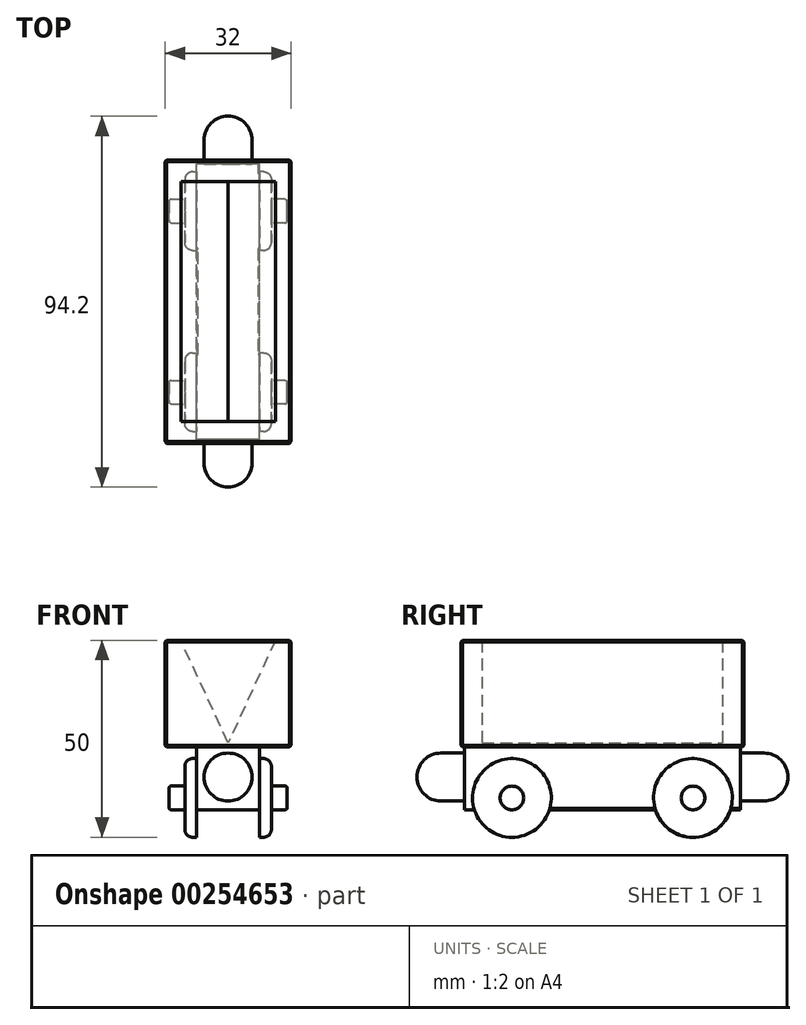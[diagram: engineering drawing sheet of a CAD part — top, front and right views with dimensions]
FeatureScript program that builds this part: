
annotation { "Feature Type Name" : "Feature", "Feature Type Description" : "" }
export const myFeature = defineFeature(function(context is Context, id is Id, definition is map)
    precondition{}
    {
        {
            var Q0;
            Q0=qCreatedBy(makeId("Front.planeOp"),FACE);
            var sketch = newSketch(context, id + "F0", { "sketchPlane" : qUnion([Q0])});
            skLineSegment(sketch, "E0.bottom", {"start": v(16, 13.5) * mm, "end": v(-16, 13.5) * mm});
            skLineSegment(sketch, "E0.top", {"start": v(16, -13.5) * mm, "end": v(-16, -13.5) * mm});
            skLineSegment(sketch, "E0.left", {"start": v(16, 13.5) * mm, "end": v(16, -13.5) * mm});
            skLineSegment(sketch, "E0.right", {"start": v(-16, 13.5) * mm, "end": v(-16, -13.5) * mm});
            skPoint(sketch, "E0.middle", {"position": v(0, 0) * mm});
            skSolve(sketch);
        }
        {
            var Q0;
            Q0 = qSketchRegion(id + "F0", true);
            extrude(context, id + "F1", {"entities" : qUnion([Q0]), "endBound" : BoundingType.SYMMETRIC, "depth" : 72 * mm});
        }
        {
            var Q0;
            Q0=makeQuery(id+"F1.opExtrude","SWEPT_FACE",FACE,{"disambiguationData":[OSD([sQuery(id+"F0.wireOp",EDGE,"E0.top")])]});
            var sketch = newSketch(context, id + "F2", { "sketchPlane" : qUnion([Q0])});
            skLineSegment(sketch, "E1.bottom", {"start": v(8, 35) * mm, "end": v(-8, 35) * mm});
            skLineSegment(sketch, "E1.top", {"start": v(8, -35) * mm, "end": v(-8, -35) * mm});
            skLineSegment(sketch, "E1.left", {"start": v(8, 35) * mm, "end": v(8, -35) * mm});
            skLineSegment(sketch, "E1.right", {"start": v(-8, 35) * mm, "end": v(-8, -35) * mm});
            skPoint(sketch, "E1.middle", {"position": v(0, 0) * mm});
            skSolve(sketch);
        }
        {
            var Q0;
            Q0 = qSketchRegion(id + "F2", true);
            extrude(context, id + "F3", {"entities" : qUnion([Q0]), "operationType" : NewBodyOperationType.ADD, "depth" : 16 * mm});
        }
        {
            var Q0;
            Q0=makeQuery(id+"F3.opExtrude","SWEPT_FACE",FACE,{"disambiguationData":[OSD([sQuery(id+"F2.wireOp",EDGE,"E1.bottom")])]});
            var sketch = newSketch(context, id + "F4", { "sketchPlane" : qUnion([Q0])});
            skCircle(sketch, "E2", {"center": v(0, -21.2) * mm, "radius": 6.1 * mm});
            skSolve(sketch);
        }
        {
            var Q0;
            Q0=makeQuery(id+"F4.imprint","IMPRINT",FACE,{"disambiguationData":[TD([[makeQuery(id+"F4.imprint","IMPRINT",EDGE,{"derivedFrom":sQuery(id+"F4.wireOp",EDGE,"E2")}),1.0]])]});
            extrude(context, id + "F5", {"entities" : qUnion([Q0]), "operationType" : NewBodyOperationType.ADD, "depth" : 6 * mm});
        }
        {
            var Q0;
            Q0=makeQuery(id+"F3.opExtrude","SWEPT_FACE",FACE,{"disambiguationData":[OSD([sQuery(id+"F2.wireOp",EDGE,"E1.top")])]});
            var sketch = newSketch(context, id + "F6", { "sketchPlane" : qUnion([Q0])});
            skCircle(sketch, "E3", {"center": v(0, -21.2) * mm, "radius": 6.1 * mm});
            skSolve(sketch);
        }
        {
            var Q0;
            Q0 = qSketchRegion(id + "F6", true);
            extrude(context, id + "F7", {"entities" : qUnion([Q0]), "operationType" : NewBodyOperationType.ADD, "depth" : 6 * mm});
        }
        {
            var Q0;
            Q0=makeQuery(id+"F5.opExtrude","CAP_FACE",FACE,{"disambiguationData":[OSD([sQuery(id+"F4.wireOp",EDGE,"E2")])],"isStart":false});
            var sketch = newSketch(context, id + "F8", { "sketchPlane" : qUnion([Q0])});
            skLineSegment(sketch, "E4", {"start": v(0, -15.1) * mm, "end": v(0, -27.3) * mm});
            skSolve(sketch);
        }
        {
            var Q0;
            {var subQ0=sQuery(id+"F8.wireOp",EDGE,"E4");Q0=makeQuery(id+"F8.imprint","IMPRINT",FACE,{"disambiguationData":[TD([[makeQuery(id+"F8.imprint","IMPRINT",EDGE,{"derivedFrom":subQ0}),-1.0]])]});}
            var Q1;
            Q1=sQuery(id+"F8.wireOp",EDGE,"E4");
            revolve(context, id + "F9", {"operationType" : NewBodyOperationType.ADD, "entities" : qUnion([Q0]), "axis" : qUnion([Q1]), "revolveType" : RevolveType.FULL});
        }
        {
            var Q0;
            Q0=makeQuery(id+"F7.opExtrude","CAP_FACE",FACE,{"disambiguationData":[OSD([sQuery(id+"F6.wireOp",EDGE,"E3")])],"isStart":false});
            var sketch = newSketch(context, id + "F10", { "sketchPlane" : qUnion([Q0])});
            skLineSegment(sketch, "E5", {"start": v(0, -15.1) * mm, "end": v(0, -27.3) * mm});
            skSolve(sketch);
        }
        {
            var Q0;
            {var subQ0=sQuery(id+"F10.wireOp",EDGE,"E5");Q0=makeQuery(id+"F10.imprint","IMPRINT",FACE,{"disambiguationData":[TD([[makeQuery(id+"F10.imprint","IMPRINT",EDGE,{"derivedFrom":subQ0}),-1.0]])]});}
            var Q1;
            Q1=sQuery(id+"F10.wireOp",EDGE,"E5");
            revolve(context, id + "F11", {"operationType" : NewBodyOperationType.ADD, "entities" : qUnion([Q0]), "axis" : qUnion([Q1]), "revolveType" : RevolveType.FULL});
        }
        {
            var Q0;
            Q0=makeQuery(id+"F3.opExtrude","SWEPT_FACE",FACE,{"disambiguationData":[OSD([sQuery(id+"F2.wireOp",EDGE,"E1.left")])]});
            var sketch = newSketch(context, id + "F12", { "sketchPlane" : qUnion([Q0])});
            skCircle(sketch, "E6", {"center": v(23, -26.5) * mm, "radius": 10 * mm});
            skSolve(sketch);
        }
        {
            var Q0;
            Q0 = qSketchRegion(id + "F12", true);
            extrude(context, id + "F13", {"entities" : qUnion([Q0]), "operationType" : NewBodyOperationType.ADD, "depth" : 3 * mm});
        }
        {
            var Q0;
            Q0=makeQuery(id+"F1.opExtrude","SWEPT_BODY",BODY,{"disambiguationData":[OSD([sQuery(id+"F0.wireOp",EDGE,"E0.bottom"),sQuery(id+"F0.wireOp",EDGE,"E0.top"),sQuery(id+"F0.wireOp",EDGE,"E0.left"),sQuery(id+"F0.wireOp",EDGE,"E0.right")])]});
            var Q1;
            Q1=qCreatedBy(makeId("Front.planeOp"),FACE);
            mirror(context, id + "F14", {"operationType" : NewBodyOperationType.ADD, "entities" : qUnion([Q0]), "mirrorPlane" : qUnion([Q1])});
        }
        {
            var Q0;
            Q0=makeQuery(id+"F1.opExtrude","SWEPT_BODY",BODY,{"disambiguationData":[OSD([sQuery(id+"F0.wireOp",EDGE,"E0.bottom"),sQuery(id+"F0.wireOp",EDGE,"E0.top"),sQuery(id+"F0.wireOp",EDGE,"E0.left"),sQuery(id+"F0.wireOp",EDGE,"E0.right")])]});
            var Q1;
            Q1=qCreatedBy(makeId("Right.planeOp"),FACE);
            mirror(context, id + "F15", {"operationType" : NewBodyOperationType.ADD, "entities" : qUnion([Q0]), "mirrorPlane" : qUnion([Q1])});
        }
        {
            var Q0;
            Q0=makeQuery(id+"F1.opExtrude","SWEPT_FACE",FACE,{"disambiguationData":[OSD([sQuery(id+"F0.wireOp",EDGE,"E0.bottom")])]});
            var sketch = newSketch(context, id + "F16", { "sketchPlane" : qUnion([Q0])});
            skLineSegment(sketch, "E7.bottom", {"start": v(12, 30.5) * mm, "end": v(-12, 30.5) * mm});
            skLineSegment(sketch, "E7.top", {"start": v(12, -30.5) * mm, "end": v(-12, -30.5) * mm});
            skLineSegment(sketch, "E7.left", {"start": v(12, 30.5) * mm, "end": v(12, -30.5) * mm});
            skLineSegment(sketch, "E7.right", {"start": v(-12, 30.5) * mm, "end": v(-12, -30.5) * mm});
            skPoint(sketch, "E7.middle", {"position": v(0, 0) * mm});
            skSolve(sketch);
        }
        {
            var Q0;
            Q0 = qSketchRegion(id + "F16", true);
            extrude(context, id + "F17", {"entities" : qUnion([Q0]), "operationType" : NewBodyOperationType.REMOVE, "oppositeDirection" : true, "depth" : 26 * mm});
        }
        {
            var Q0;
            Q0=makeQuery(id+"F14.opPattern","COPY",FACE,{"derivedFrom":makeQuery(id+"F13.opExtrude","CAP_FACE",FACE,{"disambiguationData":[OSD([sQuery(id+"F12.wireOp",EDGE,"E6")])],"isStart":false}),"instanceName":"1"});
            var sketch = newSketch(context, id + "F18", { "sketchPlane" : qUnion([Q0])});
            skCircle(sketch, "E8", {"center": v(-23, -26.5) * mm, "radius": 3 * mm});
            skSolve(sketch);
        }
        {
            var Q0;
            Q0=makeQuery(id+"F18.imprint","IMPRINT",FACE,{"disambiguationData":[TD([[makeQuery(id+"F18.imprint","IMPRINT",EDGE,{"derivedFrom":sQuery(id+"F18.wireOp",EDGE,"E8")}),1.0]])]});
            extrude(context, id + "F19", {"entities" : qUnion([Q0]), "operationType" : NewBodyOperationType.ADD, "depth" : 4 * mm});
        }
        {
            var Q0;
            Q0=makeQuery(id+"F1.opExtrude","SWEPT_BODY",BODY,{"disambiguationData":[OSD([sQuery(id+"F0.wireOp",EDGE,"E0.bottom"),sQuery(id+"F0.wireOp",EDGE,"E0.top"),sQuery(id+"F0.wireOp",EDGE,"E0.left"),sQuery(id+"F0.wireOp",EDGE,"E0.right")])]});
            var Q1;
            Q1=qCreatedBy(makeId("Front.planeOp"),FACE);
            mirror(context, id + "F20", {"operationType" : NewBodyOperationType.ADD, "entities" : qUnion([Q0]), "mirrorPlane" : qUnion([Q1])});
        }
        {
            var Q0;
            Q0=makeQuery(id+"F1.opExtrude","SWEPT_BODY",BODY,{"disambiguationData":[OSD([sQuery(id+"F0.wireOp",EDGE,"E0.bottom"),sQuery(id+"F0.wireOp",EDGE,"E0.top"),sQuery(id+"F0.wireOp",EDGE,"E0.left"),sQuery(id+"F0.wireOp",EDGE,"E0.right")])]});
            var Q1;
            Q1=qCreatedBy(makeId("Right.planeOp"),FACE);
            mirror(context, id + "F21", {"operationType" : NewBodyOperationType.ADD, "entities" : qUnion([Q0]), "mirrorPlane" : qUnion([Q1])});
        }
        {
            var Q0;
            Q0=makeQuery(id+"F17.boolean.opBoolean","COPY",FACE,{"derivedFrom":makeQuery(id+"F17.opExtrude","SWEPT_FACE",FACE,{"disambiguationData":[OSD([sQuery(id+"F16.wireOp",EDGE,"E7.bottom")])]})});
            var sketch = newSketch(context, id + "F22", { "sketchPlane" : qUnion([Q0])});
            skLineSegment(sketch, "E9", {"start": v(-12, 13.5) * mm, "end": v(-12, -12.5) * mm});
            skLineSegment(sketch, "E10", {"start": v(-12, -12.5) * mm, "end": v(0, -12.5) * mm});
            skLineSegment(sketch, "E11", {"start": v(0, -12.5) * mm, "end": v(-12, 13.5) * mm});
            skLineSegment(sketch, "E12", {"start": v(0, -12.5) * mm, "end": v(12, -12.5) * mm});
            skLineSegment(sketch, "E13", {"start": v(12, -12.5) * mm, "end": v(12, 13.5) * mm});
            skLineSegment(sketch, "E14", {"start": v(12, 13.5) * mm, "end": v(0, -12.5) * mm});
            skSolve(sketch);
        }
        {
            var Q0;
            Q0 = qSketchRegion(id + "F22", true);
            extrude(context, id + "F23", {"entities" : qUnion([Q0]), "operationType" : NewBodyOperationType.ADD, "endBound" : BoundingType.UP_TO_NEXT, "depth" : 25 * mm});
        }
        {
            var Q0;
            Q0=makeQuery(id+"F19.opExtrude","CAP_EDGE",EDGE,{"disambiguationData":[OSD([sQuery(id+"F18.wireOp",EDGE,"E8")])],"isStart":false});
            var Q1;
            Q1=makeQuery(id+"F20.opPattern","COPY",EDGE,{"derivedFrom":makeQuery(id+"F19.opExtrude","CAP_EDGE",EDGE,{"disambiguationData":[OSD([sQuery(id+"F18.wireOp",EDGE,"E8")])],"isStart":false}),"instanceName":"1"});
            var Q2;
            Q2=makeQuery(id+"F21.opPattern","COPY",EDGE,{"derivedFrom":makeQuery(id+"F20.opPattern","COPY",EDGE,{"derivedFrom":makeQuery(id+"F19.opExtrude","CAP_EDGE",EDGE,{"disambiguationData":[OSD([sQuery(id+"F18.wireOp",EDGE,"E8")])],"isStart":false}),"instanceName":"1"}),"instanceName":"1"});
            var Q3;
            Q3=makeQuery(id+"F21.opPattern","COPY",EDGE,{"derivedFrom":makeQuery(id+"F19.opExtrude","CAP_EDGE",EDGE,{"disambiguationData":[OSD([sQuery(id+"F18.wireOp",EDGE,"E8")])],"isStart":false}),"instanceName":"1"});
            fillet(context, id + "F24", {"entities" : qUnion([Q0, Q1, Q2, Q3]), "radius" : 0.5 * mm, "tangentPropagation" : true, "allowEdgeOverflow" : false});
        }
        {
            var Q0;
            Q0=makeQuery(id+"F14.opPattern","COPY",EDGE,{"derivedFrom":makeQuery(id+"F13.opExtrude","CAP_EDGE",EDGE,{"disambiguationData":[OSD([sQuery(id+"F12.wireOp",EDGE,"E6")])],"isStart":false}),"instanceName":"1"});
            var Q1;
            Q1=makeQuery(id+"F13.opExtrude","CAP_EDGE",EDGE,{"disambiguationData":[OSD([sQuery(id+"F12.wireOp",EDGE,"E6")])],"isStart":false});
            var Q2;
            Q2=makeQuery(id+"F15.opPattern","COPY",EDGE,{"derivedFrom":makeQuery(id+"F13.opExtrude","CAP_EDGE",EDGE,{"disambiguationData":[OSD([sQuery(id+"F12.wireOp",EDGE,"E6")])],"isStart":false}),"instanceName":"1"});
            var Q3;
            Q3=makeQuery(id+"F15.opPattern","COPY",EDGE,{"derivedFrom":makeQuery(id+"F14.opPattern","COPY",EDGE,{"derivedFrom":makeQuery(id+"F13.opExtrude","CAP_EDGE",EDGE,{"disambiguationData":[OSD([sQuery(id+"F12.wireOp",EDGE,"E6")])],"isStart":false}),"instanceName":"1"}),"instanceName":"1"});
            fillet(context, id + "F25", {"entities" : qUnion([Q0, Q1, Q2, Q3]), "radius" : 2 * mm, "tangentPropagation" : true, "allowEdgeOverflow" : false});
        }
        {
            var Q0;
            Q0=makeQuery(id+"F1.opExtrude","CAP_EDGE",EDGE,{"disambiguationData":[OSD([sQuery(id+"F0.wireOp",EDGE,"E0.right")])],"isStart":false});
            var Q1;
            Q1=makeQuery(id+"F1.opExtrude","CAP_EDGE",EDGE,{"disambiguationData":[OSD([sQuery(id+"F0.wireOp",EDGE,"E0.bottom")])],"isStart":false});
            var Q2;
            Q2=makeQuery(id+"F1.opExtrude","SWEPT_EDGE",EDGE,{"disambiguationData":[OSD([sQuery(id+"F0.wireOp",EDGE,"E0.bottom"),sQuery(id+"F0.wireOp",EDGE,"E0.right")])]});
            var Q3;
            Q3=makeQuery(id+"F1.opExtrude","CAP_EDGE",EDGE,{"disambiguationData":[OSD([sQuery(id+"F0.wireOp",EDGE,"E0.bottom")])],"isStart":true});
            var Q4;
            Q4=makeQuery(id+"F1.opExtrude","SWEPT_EDGE",EDGE,{"disambiguationData":[OSD([sQuery(id+"F0.wireOp",EDGE,"E0.bottom"),sQuery(id+"F0.wireOp",EDGE,"E0.left")])]});
            var Q5;
            Q5=makeQuery(id+"F1.opExtrude","CAP_EDGE",EDGE,{"disambiguationData":[OSD([sQuery(id+"F0.wireOp",EDGE,"E0.left")])],"isStart":false});
            var Q6;
            Q6=makeQuery(id+"F1.opExtrude","CAP_EDGE",EDGE,{"disambiguationData":[OSD([sQuery(id+"F0.wireOp",EDGE,"E0.top")])],"isStart":false});
            var Q7;
            Q7=makeQuery(id+"F1.opExtrude","SWEPT_EDGE",EDGE,{"disambiguationData":[OSD([sQuery(id+"F0.wireOp",EDGE,"E0.top"),sQuery(id+"F0.wireOp",EDGE,"E0.left")])]});
            var Q8;
            Q8=makeQuery(id+"F1.opExtrude","CAP_EDGE",EDGE,{"disambiguationData":[OSD([sQuery(id+"F0.wireOp",EDGE,"E0.left")])],"isStart":true});
            var Q9;
            Q9=makeQuery(id+"F1.opExtrude","CAP_FACE",FACE,{"disambiguationData":[OSD([sQuery(id+"F0.wireOp",EDGE,"E0.bottom"),sQuery(id+"F0.wireOp",EDGE,"E0.top"),sQuery(id+"F0.wireOp",EDGE,"E0.left"),sQuery(id+"F0.wireOp",EDGE,"E0.right")])],"isStart":true});
            var Q10;
            Q10=makeQuery(id+"F1.opExtrude","SWEPT_EDGE",EDGE,{"disambiguationData":[OSD([sQuery(id+"F0.wireOp",EDGE,"E0.top"),sQuery(id+"F0.wireOp",EDGE,"E0.right")])]});
            var Q11;
            {var subQ0=sQuery(id+"F12.wireOp",EDGE,"E6");var subQ1=makeQuery(id+"F13.opExtrude","CAP_FACE",FACE,{"disambiguationData":[OSD([subQ0])],"isStart":true});var subQ2=sQuery(id+"F2.wireOp",EDGE,"E1.right");var subQ3=makeQuery(id+"F13.opExtrude","SWEPT_FACE",FACE,{"disambiguationData":[OSD([subQ0])]});Q11=makeQuery(id+"F15.boolean.opBoolean","SPLIT",EDGE,{"disambiguationData":[TD([makeQuery(id+"F3.opExtrude","CAP_FACE",FACE,{"disambiguationData":[OSD([sQuery(id+"F2.wireOp",EDGE,"E1.bottom"),sQuery(id+"F2.wireOp",EDGE,"E1.top"),sQuery(id+"F2.wireOp",EDGE,"E1.left"),subQ2])],"isStart":false}),makeQuery(id+"F3.opExtrude","SWEPT_FACE",FACE,{"disambiguationData":[OSD([subQ2])]}),makeQuery(id+"F15.opPattern","COPY",FACE,{"derivedFrom":subQ3,"instanceName":"1"}),makeQuery(id+"F15.opPattern","COPY",FACE,{"derivedFrom":subQ1,"instanceName":"1"}),makeQuery(id+"F15.opPattern","COPY",FACE,{"derivedFrom":makeQuery(id+"F14.opPattern","COPY",FACE,{"derivedFrom":subQ3,"instanceName":"1"}),"instanceName":"1"}),makeQuery(id+"F15.opPattern","COPY",FACE,{"derivedFrom":makeQuery(id+"F14.opPattern","COPY",FACE,{"derivedFrom":subQ1,"instanceName":"1"}),"instanceName":"1"})])],"derivedFrom":makeQuery(id+"F3.opExtrude","CAP_EDGE",EDGE,{"disambiguationData":[OSD([subQ2])],"isStart":false})});}
            var Q12;
            {var subQ0=sQuery(id+"F12.wireOp",EDGE,"E6");var subQ1=makeQuery(id+"F13.opExtrude","CAP_FACE",FACE,{"disambiguationData":[OSD([subQ0])],"isStart":true});var subQ2=makeQuery(id+"F13.opExtrude","SWEPT_FACE",FACE,{"disambiguationData":[OSD([subQ0])]});var subQ3=sQuery(id+"F2.wireOp",EDGE,"E1.left");var subQ4=makeQuery(id+"F3.opExtrude","SWEPT_FACE",FACE,{"disambiguationData":[OSD([subQ3])]});var subQ5=sQuery(id+"F2.wireOp",EDGE,"E1.bottom");var subQ6=makeQuery(id+"F3.opExtrude","CAP_FACE",FACE,{"disambiguationData":[OSD([subQ5,sQuery(id+"F2.wireOp",EDGE,"E1.top"),subQ3,sQuery(id+"F2.wireOp",EDGE,"E1.right")])],"isStart":false});Q12=makeQuery(id+"F14.boolean.opBoolean","SPLIT",EDGE,{"disambiguationData":[TD([subQ2])],"derivedFrom":makeQuery(id+"F13.boolean.opBoolean","SPLIT",EDGE,{"disambiguationData":[TD([makeQuery(id+"F3.opExtrude","SWEPT_FACE",FACE,{"disambiguationData":[OSD([subQ5])]}),subQ6,subQ4,subQ2,subQ1])],"derivedFrom":makeQuery(id+"F3.opExtrude","CAP_EDGE",EDGE,{"disambiguationData":[OSD([subQ3])],"isStart":false})})});}
            var Q13;
            {var subQ0=sQuery(id+"F12.wireOp",EDGE,"E6");var subQ1=sQuery(id+"F2.wireOp",EDGE,"E1.left");var subQ2=sQuery(id+"F2.wireOp",EDGE,"E1.top");Q13=makeQuery(id+"F13.boolean.opBoolean","SPLIT",EDGE,{"disambiguationData":[TD([makeQuery(id+"F3.opExtrude","CAP_FACE",FACE,{"disambiguationData":[OSD([sQuery(id+"F2.wireOp",EDGE,"E1.bottom"),subQ2,subQ1,sQuery(id+"F2.wireOp",EDGE,"E1.right")])],"isStart":false}),makeQuery(id+"F3.opExtrude","SWEPT_FACE",FACE,{"disambiguationData":[OSD([subQ2])]}),makeQuery(id+"F3.opExtrude","SWEPT_FACE",FACE,{"disambiguationData":[OSD([subQ1])]}),makeQuery(id+"F13.opExtrude","SWEPT_FACE",FACE,{"disambiguationData":[OSD([subQ0])]}),makeQuery(id+"F13.opExtrude","CAP_FACE",FACE,{"disambiguationData":[OSD([subQ0])],"isStart":true})])],"derivedFrom":makeQuery(id+"F3.opExtrude","CAP_EDGE",EDGE,{"disambiguationData":[OSD([subQ1])],"isStart":false})});}
            chamfer(context, id + "F26", {"entities" : qUnion([Q0, Q1, Q2, Q3, Q4, Q5, Q6, Q7, Q8, Q9, Q10, Q11, Q12, Q13]), "width" : 0.4 * mm, "tangentPropagation" : true});
        }
    });
